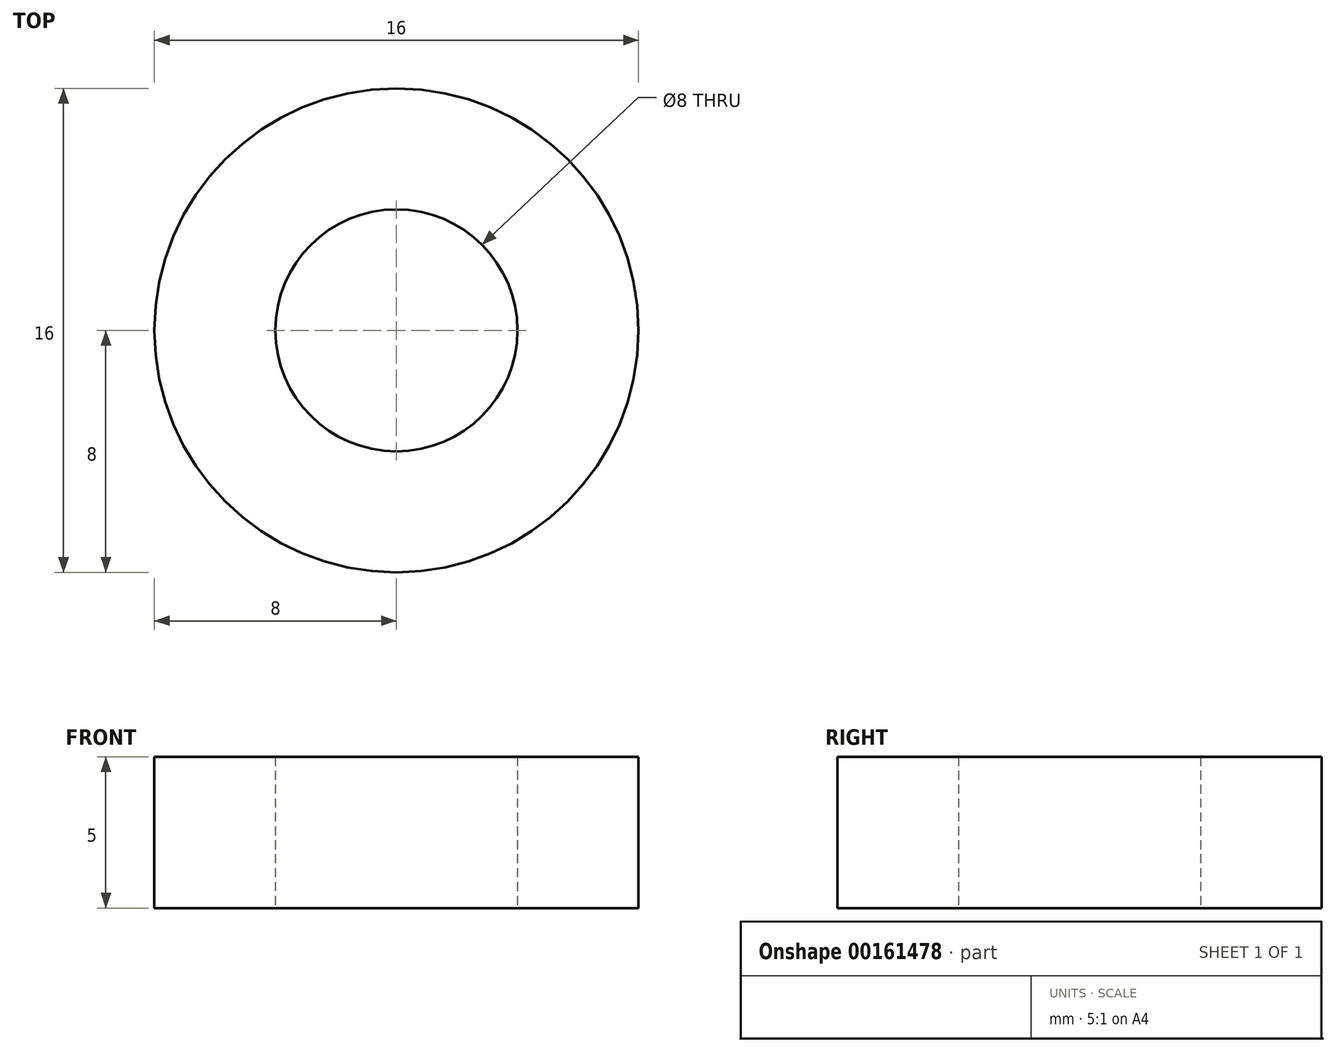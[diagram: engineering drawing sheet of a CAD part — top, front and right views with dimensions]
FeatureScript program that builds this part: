
annotation { "Feature Type Name" : "Feature", "Feature Type Description" : "" }
export const myFeature = defineFeature(function(context is Context, id is Id, definition is map)
    precondition{}
    {
        {
            var Q0;
            Q0=qCreatedBy(makeId("Top.planeOp"),FACE);
            var sketch = newSketch(context, id + "F0", { "sketchPlane" : qUnion([Q0])});
            skCircle(sketch, "E0", {"center": v(0, 0) * mm, "radius": 4 * mm});
            skCircle(sketch, "E1", {"center": v(0, 0) * mm, "radius": 8 * mm});
            skSolve(sketch);
        }
        {
            var Q0;
            Q0 = qSketchRegion(id + "F0", true);
            extrude(context, id + "F1", {"entities" : qUnion([Q0]), "depth" : 5 * mm});
        }
    });
